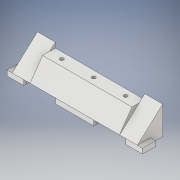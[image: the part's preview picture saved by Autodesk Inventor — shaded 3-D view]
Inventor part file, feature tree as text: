
AUTODESK INVENTOR PART (.ipt)
format: ipt  version: 2019 (Build 230136000, 136)  size: 186,880 bytes
history: native  units: mm
features: sketch x5, extrude x4, other x1, hole x1, projected_geometry x1
ambient origin geometry x8: Origin, YZ Plane, XZ Plane, XY Plane, X Axis, Y Axis, Z Axis, Center Point
bodies: Body1 (feature_tree), Body2 (feature_tree)
feature tree (12):
  other  "Твердое тело1"
  extrude  "Выдавливание1"  Depth=20.0mm
  extrude  "Выдавливание2"  Depth=4.0mm
  extrude  "Выдавливание3"  Depth=20.0mm
  extrude  "Выдавливание4"  Depth=19.0mm
  hole  "Отверстие1"  [1 undecoded]
  sketch  "Эскиз1"
  sketch  "Эскиз3"
  sketch  "Эскиз6"
  sketch  "Эскиз8"
  projected_geometry  "Спроецированная петля3"
  sketch  "Эскиз10"
note: 1 required parameter value undecoded (feature->parameter linkage not recoverable at this tier; creation-order binding heuristic only, values carry confidence <= 0.55)
